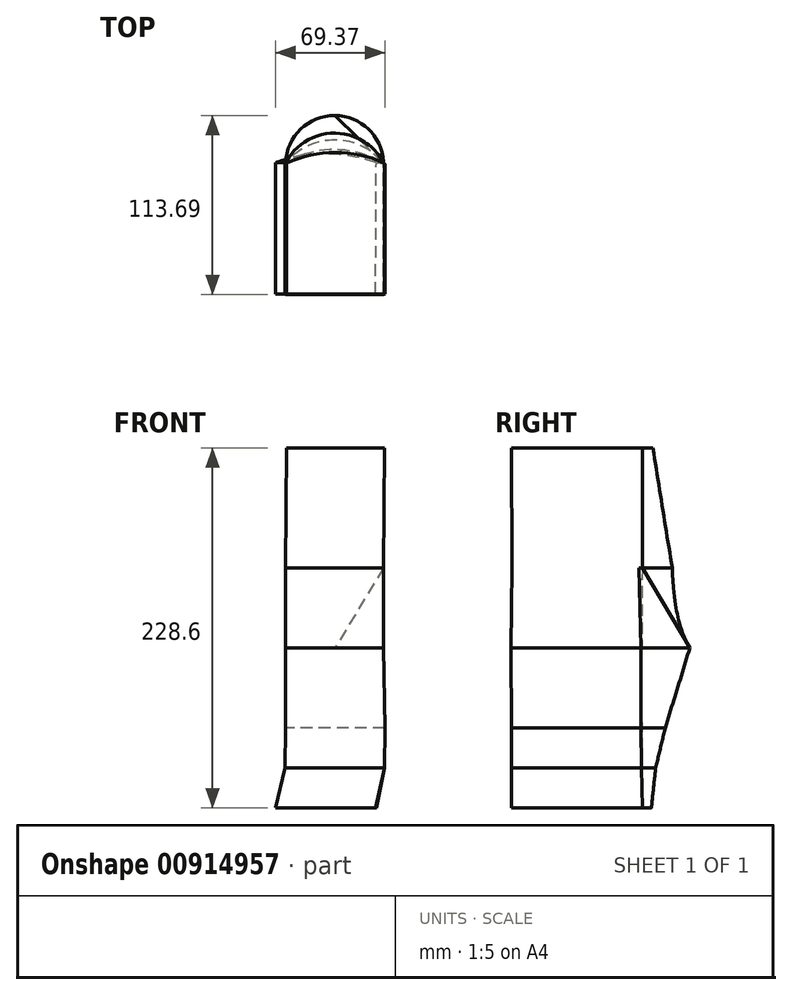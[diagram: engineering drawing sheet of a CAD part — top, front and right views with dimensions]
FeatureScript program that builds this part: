
annotation { "Feature Type Name" : "Feature", "Feature Type Description" : "" }
export const myFeature = defineFeature(function(context is Context, id is Id, definition is map)
    precondition{}
    {
        {
            var Q0;
            Q0=qCreatedBy(makeId("Top.planeOp"),FACE);
            var sketch = newSketch(context, id + "F0", { "sketchPlane" : qUnion([Q0])});
            skLineSegment(sketch, "E0", {"start": v(-37.57, -70.02) * mm, "end": v(-37.57, 13.36) * mm});
            skArc(sketch, "E1", {"start": v(26.34, 13.36) * mm, "mid": v(-5.61, 18.88) * mm, "end": v(-37.57, 13.36) * mm});
            skLineSegment(sketch, "E2", {"start": v(-37.57, -70.02) * mm, "end": v(25.93, -70.02) * mm});
            skLineSegment(sketch, "E3", {"start": v(25.93, -70.02) * mm, "end": v(26.34, 13.36) * mm});
            skSolve(sketch);
        }
        {
            var Q0;
            Q0=qCreatedBy(makeId("Top.planeOp"),FACE);
            cPlane(context, id + "F1", {"entities" : qUnion([Q0]), "cplaneType" : CPlaneType.OFFSET, "offset" : 25.4 * mm, "width" : 152.4 * mm, "height" : 152.4 * mm});
        }
        {
            var Q0;
            Q0=qCreatedBy(id+"F1.planeOp",FACE);
            var sketch = newSketch(context, id + "F2", { "sketchPlane" : qUnion([Q0])});
            skLineSegment(sketch, "E4", {"start": v(-31.5, 13.27) * mm, "end": v(-31.5, -69.82) * mm});
            skLineSegment(sketch, "E5", {"start": v(-31.5, -69.82) * mm, "end": v(31.7, -69.82) * mm});
            skLineSegment(sketch, "E6", {"start": v(31.7, -69.82) * mm, "end": v(31.7, 12.71) * mm});
            skArc(sketch, "E7", {"start": v(31.7, 12.71) * mm, "mid": v(0.18, 21.61) * mm, "end": v(-31.5, 13.27) * mm});
            skSolve(sketch);
        }
        {
            var Q0;
            Q0=makeQuery(id+"F0.imprint","IMPRINT",FACE,{"disambiguationData":[TD([[makeQuery(id+"F0.imprint","IMPRINT",EDGE,{"derivedFrom":sQuery(id+"F0.wireOp",EDGE,"E0")}),-1.0]])]});
            var Q1;
            Q1=makeQuery(id+"F2.imprint","IMPRINT",FACE,{"disambiguationData":[TD([[makeQuery(id+"F2.imprint","IMPRINT",EDGE,{"derivedFrom":sQuery(id+"F2.wireOp",EDGE,"E4")}),1.0]])]});
            loft(context, id + "F3", {"sheetProfilesArray" : [{ "sheetProfileEntities" : qUnion([Q0]) }, { "sheetProfileEntities" : qUnion([Q1]) }]});
        }
        {
            var Q0;
            Q0=qCreatedBy(id+"F1.planeOp",FACE);
            cPlane(context, id + "F4", {"entities" : qUnion([Q0]), "cplaneType" : CPlaneType.OFFSET, "offset" : 25.4 * mm, "width" : 152.4 * mm, "height" : 152.4 * mm});
        }
        {
            var Q0;
            Q0=qCreatedBy(id+"F4.planeOp",FACE);
            var sketch = newSketch(context, id + "F5", { "sketchPlane" : qUnion([Q0])});
            skLineSegment(sketch, "E8", {"start": v(-31.23, 13.1) * mm, "end": v(-31.23, -70.08) * mm});
            skLineSegment(sketch, "E9", {"start": v(-31.23, -70.08) * mm, "end": v(31.8, -70.08) * mm});
            skLineSegment(sketch, "E10", {"start": v(31.8, -70.08) * mm, "end": v(31.8, 12.23) * mm});
            skArc(sketch, "E11", {"start": v(31.8, 12.23) * mm, "mid": v(0.5, 27.74) * mm, "end": v(-31.23, 13.1) * mm});
            skSolve(sketch);
        }
        {
            var Q1;
            Q1=makeQuery(id+"F3.opLoft","CAP_FACE",FACE,{"disambiguationData":[OSD([makeQuery(id+"F2.imprint","IMPRINT",FACE,{"disambiguationData":[TD([[makeQuery(id+"F2.imprint","IMPRINT",EDGE,{"derivedFrom":sQuery(id+"F2.wireOp",EDGE,"E4")}),1.0]])]})])],"isStart":true});
            var Q2;
            Q2=makeQuery(id+"F5.imprint","IMPRINT",FACE,{"disambiguationData":[TD([[makeQuery(id+"F5.imprint","IMPRINT",EDGE,{"derivedFrom":sQuery(id+"F5.wireOp",EDGE,"E8")}),1.0]])]});
            loft(context, id + "F6", {"operationType" : NewBodyOperationType.ADD, "sheetProfilesArray" : [{ "sheetProfileEntities" : qUnion([Q1]) }, { "sheetProfileEntities" : qUnion([Q2]) }]});
        }
        {
            var Q0;
            Q0=qCreatedBy(id+"F4.planeOp",FACE);
            cPlane(context, id + "F7", {"entities" : qUnion([Q0]), "cplaneType" : CPlaneType.OFFSET, "offset" : 50.8 * mm, "width" : 152.4 * mm, "height" : 152.4 * mm});
        }
        {
            var Q0;
            Q0=qCreatedBy(id+"F7.planeOp",FACE);
            var sketch = newSketch(context, id + "F8", { "sketchPlane" : qUnion([Q0])});
            skLineSegment(sketch, "E12", {"start": v(-31.23, 12.8) * mm, "end": v(-31.23, -70.37) * mm});
            skLineSegment(sketch, "E13", {"start": v(-31.23, -70.37) * mm, "end": v(30.94, -70.37) * mm});
            skLineSegment(sketch, "E14", {"start": v(30.94, -70.37) * mm, "end": v(30.94, 12.23) * mm});
            skArc(sketch, "E15", {"start": v(30.94, 12.23) * mm, "mid": v(0.14, 43.32) * mm, "end": v(-31.23, 12.8) * mm});
            skSolve(sketch);
        }
        {
            var Q1;
            Q1=makeQuery(id+"F6.opLoft","CAP_FACE",FACE,{"disambiguationData":[OSD([makeQuery(id+"F5.imprint","IMPRINT",FACE,{"disambiguationData":[TD([[makeQuery(id+"F5.imprint","IMPRINT",EDGE,{"derivedFrom":sQuery(id+"F5.wireOp",EDGE,"E8")}),1.0]])]})])],"isStart":true});
            var Q2;
            Q2=makeQuery(id+"F8.imprint","IMPRINT",FACE,{"disambiguationData":[TD([[makeQuery(id+"F8.imprint","IMPRINT",EDGE,{"derivedFrom":sQuery(id+"F8.wireOp",EDGE,"E12")}),1.0]])]});
            loft(context, id + "F9", {"operationType" : NewBodyOperationType.ADD, "sheetProfilesArray" : [{ "sheetProfileEntities" : qUnion([Q1]) }, { "sheetProfileEntities" : qUnion([Q2]) }]});
        }
        {
            var Q0;
            Q0=qCreatedBy(id+"F7.planeOp",FACE);
            cPlane(context, id + "F10", {"entities" : qUnion([Q0]), "cplaneType" : CPlaneType.OFFSET, "offset" : 50.8 * mm, "width" : 152.4 * mm, "height" : 152.4 * mm});
        }
        {
            var Q0;
            Q0=qCreatedBy(id+"F10.planeOp",FACE);
            var sketch = newSketch(context, id + "F11", { "sketchPlane" : qUnion([Q0])});
            skLineSegment(sketch, "E16", {"start": v(-31.23, 13.1) * mm, "end": v(-31.23, -69.5) * mm});
            skLineSegment(sketch, "E17", {"start": v(-31.23, -69.5) * mm, "end": v(30.94, -69.5) * mm});
            skLineSegment(sketch, "E18", {"start": v(30.94, -69.5) * mm, "end": v(30.94, 11.08) * mm});
            skArc(sketch, "E19", {"start": v(30.94, 13.1) * mm, "mid": v(-0.14, 32.17) * mm, "end": v(-31.23, 13.1) * mm});
            skLineSegment(sketch, "E20", {"start": v(30.94, 13.1) * mm, "end": v(30.94, 11.08) * mm});
            skSolve(sketch);
        }
        {
            var Q1;
            Q1=makeQuery(id+"F11.imprint","IMPRINT",FACE,{"disambiguationData":[TD([[makeQuery(id+"F11.imprint","IMPRINT",EDGE,{"derivedFrom":sQuery(id+"F11.wireOp",EDGE,"E16")}),1.0]])]});
            var Q2;
            Q2=makeQuery(id+"F9.opLoft","CAP_FACE",FACE,{"disambiguationData":[OSD([makeQuery(id+"F8.imprint","IMPRINT",FACE,{"disambiguationData":[TD([[makeQuery(id+"F8.imprint","IMPRINT",EDGE,{"derivedFrom":sQuery(id+"F8.wireOp",EDGE,"E12")}),1.0]])]})])],"isStart":true});
            loft(context, id + "F12", {"operationType" : NewBodyOperationType.ADD, "sheetProfilesArray" : [{ "sheetProfileEntities" : qUnion([Q1]) }, { "sheetProfileEntities" : qUnion([Q2]) }]});
        }
        {
            var Q0;
            Q0=qCreatedBy(id+"F10.planeOp",FACE);
            cPlane(context, id + "F13", {"entities" : qUnion([Q0]), "cplaneType" : CPlaneType.OFFSET, "offset" : 76.2 * mm, "width" : 152.4 * mm, "height" : 152.4 * mm});
        }
        {
            var Q0;
            Q0=qCreatedBy(id+"F13.planeOp",FACE);
            var sketch = newSketch(context, id + "F14", { "sketchPlane" : qUnion([Q0])});
            skLineSegment(sketch, "E21", {"start": v(-30.65, 13.1) * mm, "end": v(-30.65, -70.08) * mm});
            skLineSegment(sketch, "E22", {"start": v(-30.65, -70.08) * mm, "end": v(31.51, -70.08) * mm});
            skLineSegment(sketch, "E23", {"start": v(31.51, -70.08) * mm, "end": v(31.51, 13.1) * mm});
            skArc(sketch, "E24", {"start": v(31.51, 13.1) * mm, "mid": v(0.43, 19.9) * mm, "end": v(-30.65, 13.1) * mm});
            skSolve(sketch);
        }
        {
            var Q1;
            Q1=makeQuery(id+"F12.opLoft","CAP_FACE",FACE,{"disambiguationData":[OSD([makeQuery(id+"F11.imprint","IMPRINT",FACE,{"disambiguationData":[TD([[makeQuery(id+"F11.imprint","IMPRINT",EDGE,{"derivedFrom":sQuery(id+"F11.wireOp",EDGE,"E16")}),1.0]])]})])],"isStart":true});
            var Q2;
            Q2=makeQuery(id+"F14.imprint","IMPRINT",FACE,{"disambiguationData":[TD([[makeQuery(id+"F14.imprint","IMPRINT",EDGE,{"derivedFrom":sQuery(id+"F14.wireOp",EDGE,"E21")}),1.0]])]});
            loft(context, id + "F15", {"operationType" : NewBodyOperationType.ADD, "sheetProfilesArray" : [{ "sheetProfileEntities" : qUnion([Q1]) }, { "sheetProfileEntities" : qUnion([Q2]) }]});
        }
    });
